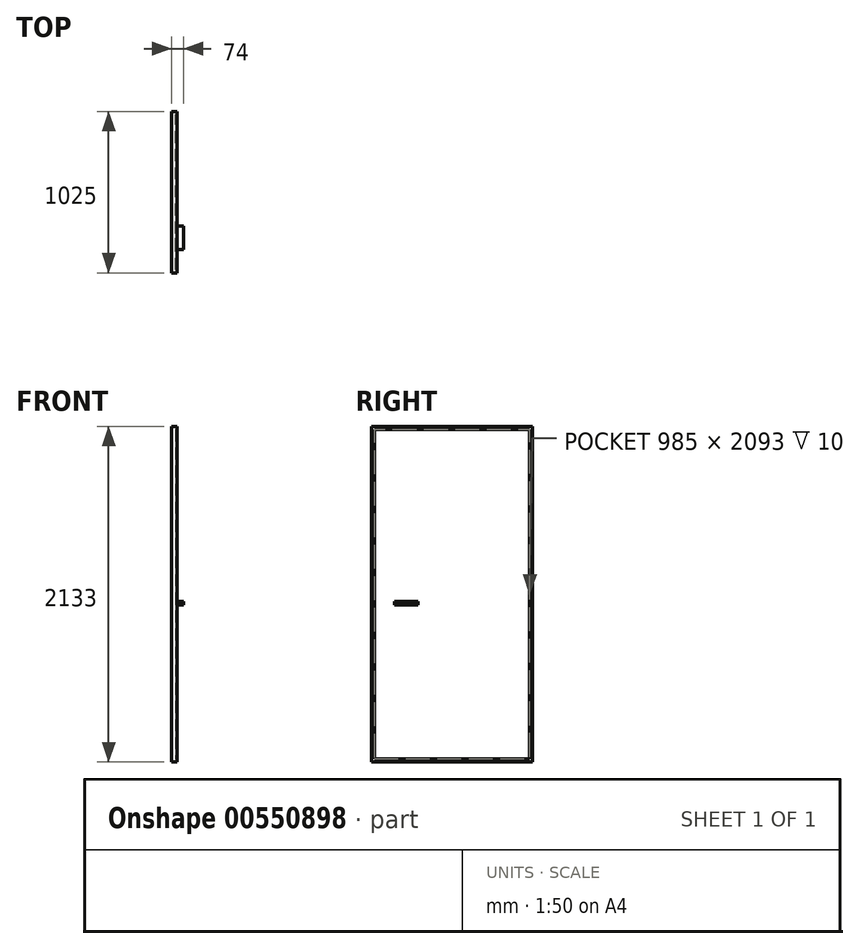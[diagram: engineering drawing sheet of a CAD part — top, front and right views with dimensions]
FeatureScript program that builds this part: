
annotation { "Feature Type Name" : "Feature", "Feature Type Description" : "" }
export const myFeature = defineFeature(function(context is Context, id is Id, definition is map)
    precondition{}
    {
        {
            var Q0;
            Q0=qCreatedBy(makeId("Right.planeOp"),FACE);
            var sketch = newSketch(context, id + "F0", { "sketchPlane" : qUnion([Q0])});
            skLineSegment(sketch, "E0.bottom", {"start": v(0, 0) * mm, "end": v(1025, 0) * mm});
            skLineSegment(sketch, "E0.top", {"start": v(0, 2133) * mm, "end": v(1025, 2133) * mm});
            skLineSegment(sketch, "E0.left", {"start": v(0, 0) * mm, "end": v(0, 2133) * mm});
            skLineSegment(sketch, "E0.right", {"start": v(1025, 0) * mm, "end": v(1025, 2133) * mm});
            skSolve(sketch);
        }
        {
            var Q0;
            Q0=makeQuery(id+"F0.imprint","IMPRINT",FACE,{"disambiguationData":[TD([[makeQuery(id+"F0.imprint","IMPRINT",EDGE,{"derivedFrom":sQuery(id+"F0.wireOp",EDGE,"E0.bottom")}),1.0]])]});
            extrude(context, id + "F1", {"entities" : qUnion([Q0]), "depth" : 24 * mm, "offsetDistance" : 25 * mm});
        }
        {
            var Q0;
            Q0=makeQuery(id+"F1.opExtrude","CAP_FACE",FACE,{"disambiguationData":[OSD([sQuery(id+"F0.wireOp",EDGE,"E0.bottom"),sQuery(id+"F0.wireOp",EDGE,"E0.top"),sQuery(id+"F0.wireOp",EDGE,"E0.left"),sQuery(id+"F0.wireOp",EDGE,"E0.right")])],"isStart":false});
            var sketch = newSketch(context, id + "F2", { "sketchPlane" : qUnion([Q0])});
            skLineSegment(sketch, "E1.bottom", {"start": v(146.84, 1020) * mm, "end": v(296.84, 1020) * mm});
            skLineSegment(sketch, "E1.top", {"start": v(146.84, 1000) * mm, "end": v(296.84, 1000) * mm});
            skLineSegment(sketch, "E1.left", {"start": v(146.84, 1020) * mm, "end": v(146.84, 1000) * mm});
            skLineSegment(sketch, "E1.right", {"start": v(296.84, 1020) * mm, "end": v(296.84, 1000) * mm});
            skSolve(sketch);
        }
        {
            var Q0;
            Q0=makeQuery(id+"F2.imprint","IMPRINT",FACE,{"disambiguationData":[TD([[makeQuery(id+"F2.imprint","IMPRINT",EDGE,{"derivedFrom":sQuery(id+"F2.wireOp",EDGE,"E1.bottom")}),-1.0]])]});
            extrude(context, id + "F3", {"entities" : qUnion([Q0]), "depth" : 50 * mm, "offsetDistance" : 25 * mm});
        }
        {
            var Q0;
            Q0=makeQuery(id+"F1.opExtrude","CAP_FACE",FACE,{"disambiguationData":[OSD([sQuery(id+"F0.wireOp",EDGE,"E0.bottom"),sQuery(id+"F0.wireOp",EDGE,"E0.top"),sQuery(id+"F0.wireOp",EDGE,"E0.left"),sQuery(id+"F0.wireOp",EDGE,"E0.right")])],"isStart":false});
            var sketch = newSketch(context, id + "F4", { "sketchPlane" : qUnion([Q0])});
            skLineSegment(sketch, "E2.bottom", {"start": v(20, 2113) * mm, "end": v(1005, 2113) * mm});
            skLineSegment(sketch, "E2.top", {"start": v(20, 20) * mm, "end": v(1005, 20) * mm});
            skLineSegment(sketch, "E2.left", {"start": v(20, 2113) * mm, "end": v(20, 20) * mm});
            skLineSegment(sketch, "E2.right", {"start": v(1005, 2113) * mm, "end": v(1005, 20) * mm});
            skLineSegment(sketch, "E3.bottom", {"start": v(0, 2133) * mm, "end": v(1025, 2133) * mm});
            skLineSegment(sketch, "E3.top", {"start": v(0, 0) * mm, "end": v(1025, 0) * mm});
            skLineSegment(sketch, "E3.left", {"start": v(0, 2133) * mm, "end": v(0, 0) * mm});
            skLineSegment(sketch, "E3.right", {"start": v(1025, 2133) * mm, "end": v(1025, 0) * mm});
            skSolve(sketch);
        }
        {
            var Q0;
            Q0 = qSketchRegion(id + "F4", true);
            extrude(context, id + "F5", {"entities" : qUnion([Q0]), "operationType" : NewBodyOperationType.ADD, "depth" : 10 * mm, "offsetDistance" : 25 * mm});
        }
    });
